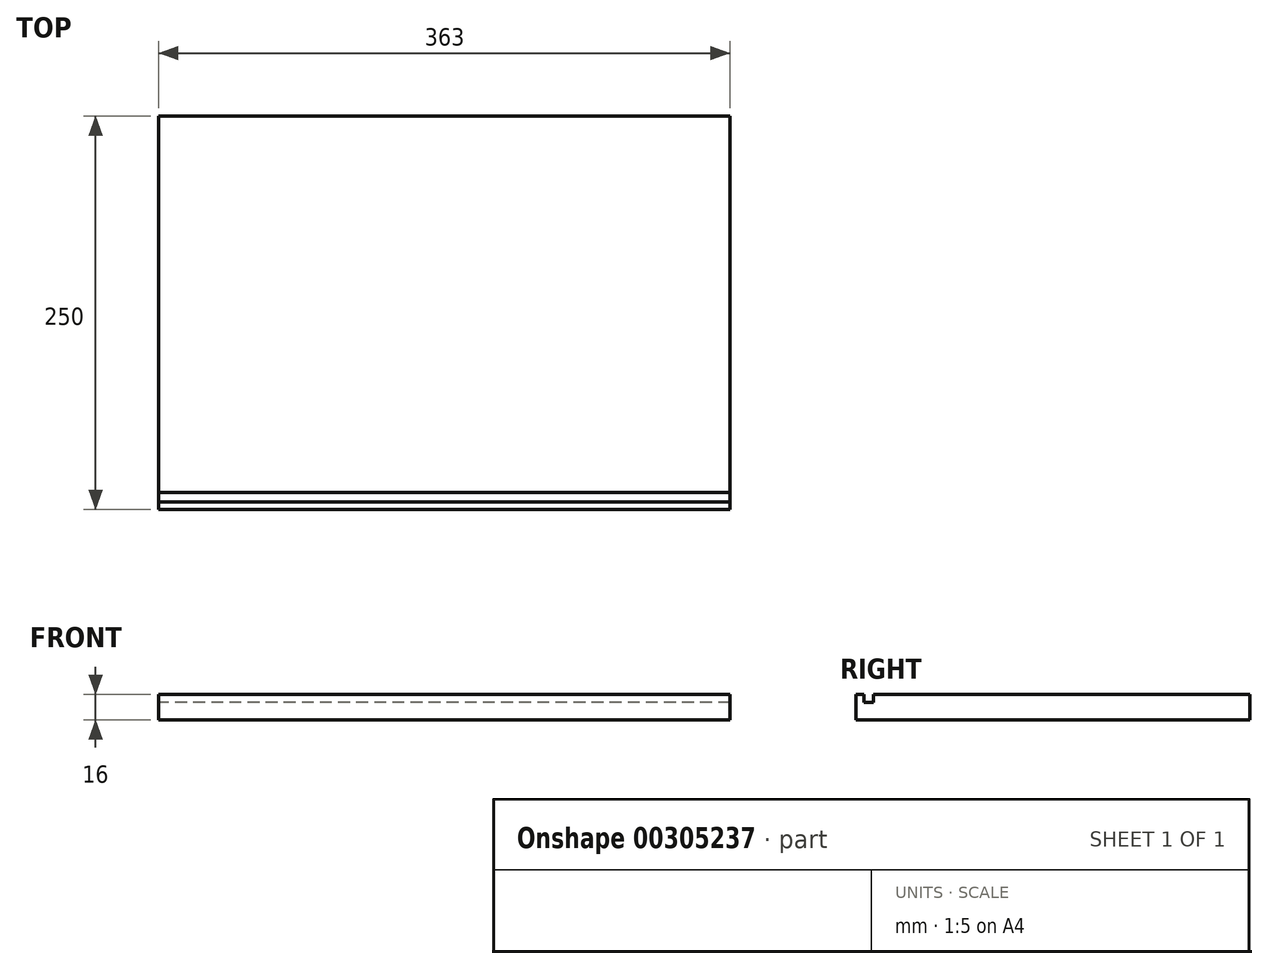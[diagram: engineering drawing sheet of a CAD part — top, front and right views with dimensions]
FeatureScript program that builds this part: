
annotation { "Feature Type Name" : "Feature", "Feature Type Description" : "" }
export const myFeature = defineFeature(function(context is Context, id is Id, definition is map)
    precondition{}
    {
        {
            var Q0;
            Q0=qCreatedBy(makeId("Right.planeOp"),FACE);
            var sketch = newSketch(context, id + "F0", { "sketchPlane" : qUnion([Q0])});
            skLineSegment(sketch, "E0", {"start": v(-125, 16) * mm, "end": v(-125, 0) * mm});
            skLineSegment(sketch, "E1", {"start": v(-125, 0) * mm, "end": v(125, 0) * mm});
            skLineSegment(sketch, "E2", {"start": v(125, 0) * mm, "end": v(125, 16) * mm});
            skLineSegment(sketch, "E3", {"start": v(125, 16) * mm, "end": v(-114, 16) * mm});
            skLineSegment(sketch, "E4", {"start": v(-114, 16) * mm, "end": v(-114, 11) * mm});
            skLineSegment(sketch, "E5", {"start": v(-114, 11) * mm, "end": v(-120, 11) * mm});
            skLineSegment(sketch, "E6", {"start": v(-120, 11) * mm, "end": v(-120, 16) * mm});
            skLineSegment(sketch, "E7", {"start": v(-120, 16) * mm, "end": v(-125, 16) * mm});
            skSolve(sketch);
        }
        {
            var Q0;
            Q0=makeQuery(id+"F0.imprint","IMPRINT",FACE,{"disambiguationData":[TD([[makeQuery(id+"F0.imprint","IMPRINT",EDGE,{"derivedFrom":sQuery(id+"F0.wireOp",EDGE,"E0")}),1.0]])]});
            extrude(context, id + "F1", {"entities" : qUnion([Q0]), "endBound" : BoundingType.SYMMETRIC, "depth" : 363 * mm});
        }
    });
